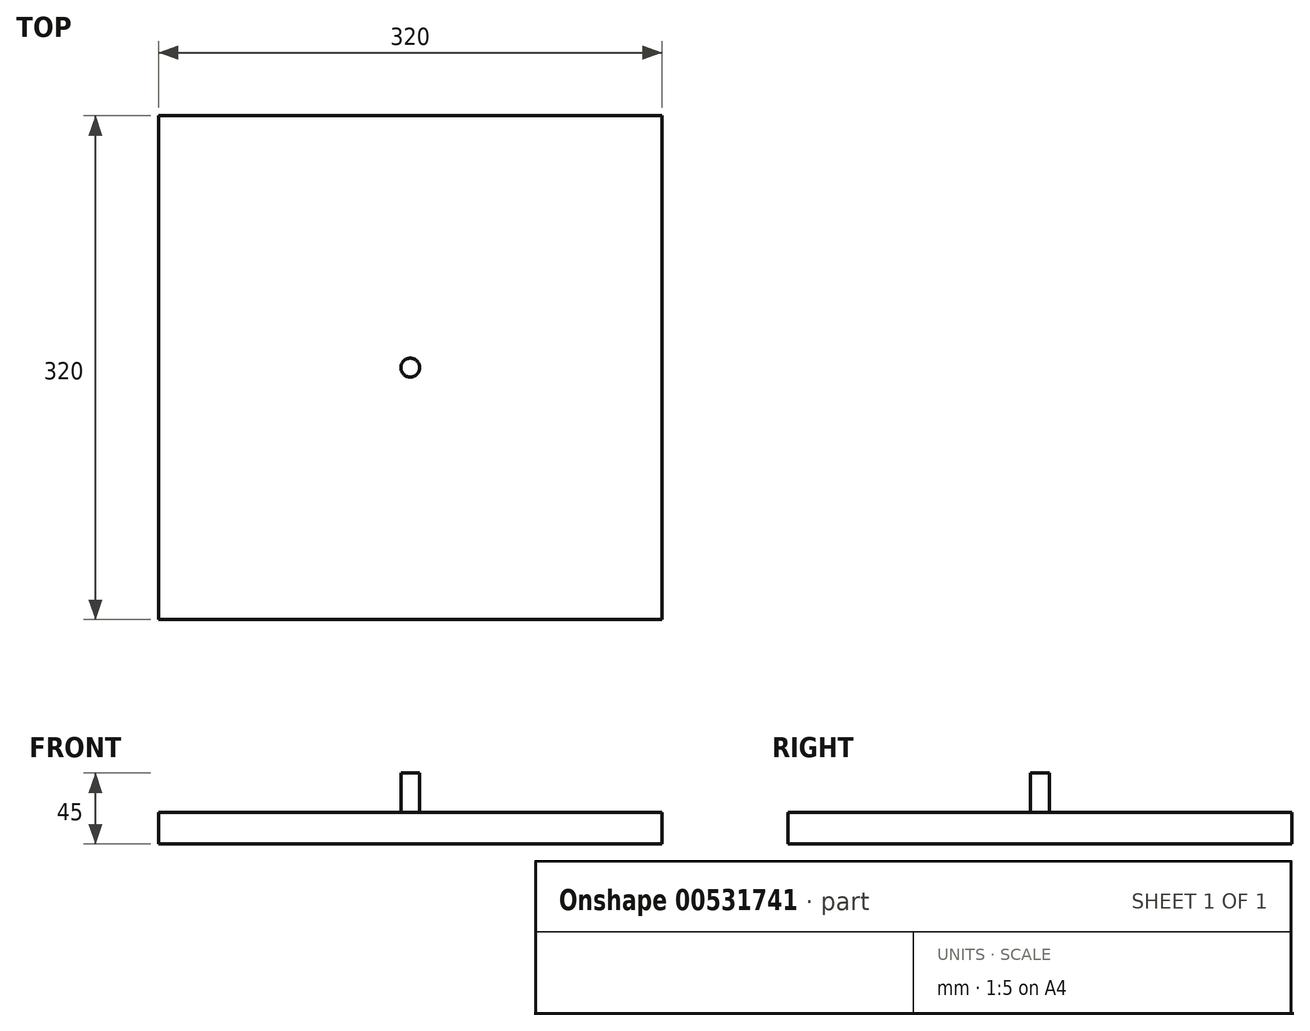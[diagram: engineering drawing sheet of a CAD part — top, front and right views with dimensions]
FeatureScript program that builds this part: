
annotation { "Feature Type Name" : "Feature", "Feature Type Description" : "" }
export const myFeature = defineFeature(function(context is Context, id is Id, definition is map)
    precondition{}
    {
        {
            var Q0;
            Q0=qCreatedBy(makeId("Top.planeOp"),FACE);
            var sketch = newSketch(context, id + "F0", { "sketchPlane" : qUnion([Q0])});
            skLineSegment(sketch, "E0.bottom", {"start": v(160, 160) * mm, "end": v(-160, 160) * mm});
            skLineSegment(sketch, "E0.top", {"start": v(160, -160) * mm, "end": v(-160, -160) * mm});
            skLineSegment(sketch, "E0.left", {"start": v(160, 160) * mm, "end": v(160, -160) * mm});
            skLineSegment(sketch, "E0.right", {"start": v(-160, 160) * mm, "end": v(-160, -160) * mm});
            skPoint(sketch, "E0.middle", {"position": v(0, 0) * mm});
            skSolve(sketch);
        }
        {
            var Q0;
            Q0=makeQuery(id+"F0.imprint","IMPRINT",FACE,{"disambiguationData":[TD([[makeQuery(id+"F0.imprint","IMPRINT",EDGE,{"derivedFrom":sQuery(id+"F0.wireOp",EDGE,"E0.bottom")}),1.0]])]});
            extrude(context, id + "F1", {"entities" : qUnion([Q0]), "depth" : 20 * mm, "offsetDistance" : 25 * mm});
        }
        {
            var Q0;
            Q0=makeQuery(id+"F1.opExtrude","CAP_FACE",FACE,{"disambiguationData":[OSD([sQuery(id+"F0.wireOp",EDGE,"E0.bottom"),sQuery(id+"F0.wireOp",EDGE,"E0.top"),sQuery(id+"F0.wireOp",EDGE,"E0.left"),sQuery(id+"F0.wireOp",EDGE,"E0.right")])],"isStart":false});
            var sketch = newSketch(context, id + "F2", { "sketchPlane" : qUnion([Q0])});
            skLineSegment(sketch, "E1", {"start": v(0, 0) * mm, "end": v(0, -115) * mm});
            skCircle(sketch, "E2", {"center": v(0, 0) * mm, "radius": 115 * mm});
            skCircle(sketch, "E3", {"center": v(0, 0) * mm, "radius": 6 * mm});
            skSolve(sketch);
        }
        {
            var Q0;
            Q0=makeQuery(id+"F2.imprint","IMPRINT",FACE,{"disambiguationData":[TD([[makeQuery(id+"F2.imprint","IMPRINT",EDGE,{"derivedFrom":sQuery(id+"F2.wireOp",EDGE,"E3")}),1.0]])]});
            extrude(context, id + "F3", {"entities" : qUnion([Q0]), "operationType" : NewBodyOperationType.ADD, "depth" : 25 * mm, "offsetDistance" : 25 * mm});
        }
    });
